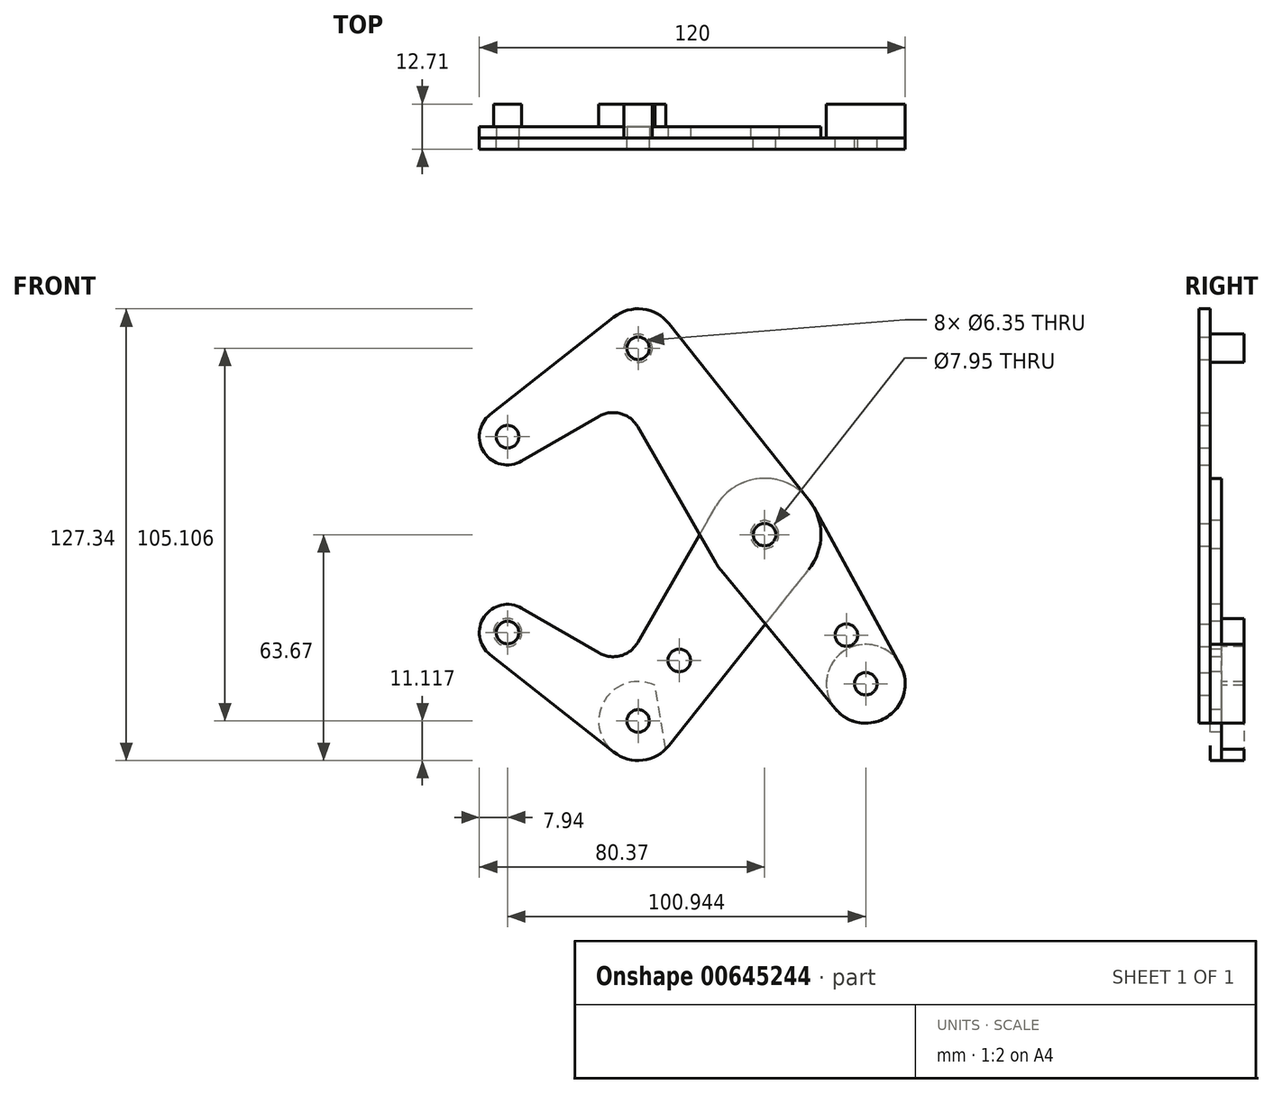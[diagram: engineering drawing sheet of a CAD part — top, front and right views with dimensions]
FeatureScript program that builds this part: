
annotation { "Feature Type Name" : "Feature", "Feature Type Description" : "" }
export const myFeature = defineFeature(function(context is Context, id is Id, definition is map)
    precondition{}
    {
        {
            var Q0;
            Q0=qCreatedBy(makeId("Front.planeOp"),FACE);
            var sketch = newSketch(context, id + "F0", { "sketchPlane" : qUnion([Q0])});
            skLineSegment(sketch, "E0", {"start": v(-35.64, 52.55) * mm, "end": v(-72.43, 27.6) * mm, "construction": true});
            skLineSegment(sketch, "E1", {"start": v(-35.64, 52.55) * mm, "end": v(28.51, -42.04) * mm, "construction": true});
            skCircle(sketch, "E2", {"center": v(-35.64, 52.55) * mm, "radius": 11.11 * mm});
            skCircle(sketch, "E3", {"center": v(-72.43, 27.6) * mm, "radius": 7.94 * mm});
            skCircle(sketch, "E4", {"center": v(-72.43, 27.6) * mm, "radius": 3.18 * mm});
            skCircle(sketch, "E5", {"center": v(-35.64, 52.55) * mm, "radius": 3.18 * mm});
            skCircle(sketch, "E6", {"center": v(0, 0) * mm, "radius": 15.88 * mm});
            skCircle(sketch, "E7", {"center": v(0, 0) * mm, "radius": 3.18 * mm});
            skCircle(sketch, "E8", {"center": v(0, 0) * mm, "radius": 3.98 * mm});
            skCircle(sketch, "E9", {"center": v(28.51, -42.04) * mm, "radius": 11.11 * mm});
            skCircle(sketch, "E10", {"center": v(28.51, -42.04) * mm, "radius": 3.18 * mm});
            skCircle(sketch, "E11", {"center": v(23.05, -28.33) * mm, "radius": 3.18 * mm});
            skLineSegment(sketch, "E12", {"start": v(0, 0) * mm, "end": v(-35.64, -52.55) * mm, "construction": true});
            skLineSegment(sketch, "E13", {"start": v(-77.34, 33.84) * mm, "end": v(-42.52, 61.28) * mm});
            skLineSegment(sketch, "E14", {"start": v(-68.46, 20.73) * mm, "end": v(-46.64, 33.35) * mm});
            skLineSegment(sketch, "E15", {"start": v(-26.94, 59.46) * mm, "end": v(12.43, 9.87) * mm});
            skLineSegment(sketch, "E16", {"start": v(-35.76, 30.43) * mm, "end": v(-13.77, -7.9) * mm});
            skLineSegment(sketch, "E17", {"start": v(-12.25, -10.1) * mm, "end": v(19.94, -49.11) * mm});
            skLineSegment(sketch, "E18", {"start": v(38.26, -36.7) * mm, "end": v(13.92, 7.64) * mm});
            skArc(sketch, "E19.filletArc", {"start": v(-35.76, 30.43) * mm, "mid": v(-40.6, 34.15) * mm, "end": v(-46.64, 33.35) * mm});
            skCircle(sketch, "E20", {"center": v(-35.64, -52.55) * mm, "radius": 3.18 * mm});
            skCircle(sketch, "E21", {"center": v(-35.64, -52.55) * mm, "radius": 11.11 * mm});
            skCircle(sketch, "E22", {"center": v(-24.05, -35.46) * mm, "radius": 3.18 * mm});
            skLineSegment(sketch, "E23", {"start": v(-35.64, -52.55) * mm, "end": v(-72.43, -27.6) * mm, "construction": true});
            skCircle(sketch, "E24", {"center": v(-72.43, -27.6) * mm, "radius": 7.94 * mm});
            skCircle(sketch, "E25", {"center": v(-72.43, -27.6) * mm, "radius": 3.18 * mm});
            skLineSegment(sketch, "E26", {"start": v(-68.46, -20.73) * mm, "end": v(-46.64, -33.35) * mm});
            skLineSegment(sketch, "E27", {"start": v(-77.34, -33.84) * mm, "end": v(-42.52, -61.28) * mm});
            skLineSegment(sketch, "E28", {"start": v(-35.76, -30.43) * mm, "end": v(-13.77, 7.9) * mm});
            skLineSegment(sketch, "E29", {"start": v(-26.94, -59.46) * mm, "end": v(12.43, -9.87) * mm});
            skArc(sketch, "E30.filletArc", {"start": v(-46.64, -33.35) * mm, "mid": v(-40.6, -34.15) * mm, "end": v(-35.76, -30.43) * mm});
            skSolve(sketch);
        }
        {
            var Q0;
            {var subQ4=sQuery(id+"F0.wireOp",EDGE,"E13");Q0=makeQuery(id+"F0.imprint","IMPRINT",FACE,{"disambiguationData":[TD([[makeQuery(id+"F0.imprint","IMPRINT",EDGE,{"derivedFrom":subQ4}),-1.0]])]});}
            var Q1;
            Q1=makeQuery(id+"F0.imprint","IMPRINT",FACE,{"disambiguationData":[TD([[makeQuery(id+"F0.imprint","IMPRINT",EDGE,{"derivedFrom":sQuery(id+"F0.wireOp",EDGE,"E4")}),-1.0]])]});
            var Q2;
            Q2=makeQuery(id+"F0.imprint","IMPRINT",FACE,{"disambiguationData":[TD([[makeQuery(id+"F0.imprint","IMPRINT",EDGE,{"derivedFrom":sQuery(id+"F0.wireOp",EDGE,"E5")}),-1.0]])]});
            var Q3;
            Q3=makeQuery(id+"F0.imprint","IMPRINT",FACE,{"disambiguationData":[TD([[makeQuery(id+"F0.imprint","IMPRINT",EDGE,{"derivedFrom":sQuery(id+"F0.wireOp",EDGE,"E8")}),-1.0]])]});
            var Q4;
            Q4=makeQuery(id+"F0.imprint","IMPRINT",FACE,{"disambiguationData":[TD([[makeQuery(id+"F0.imprint","IMPRINT",EDGE,{"derivedFrom":sQuery(id+"F0.wireOp",EDGE,"E11")}),-1.0]])]});
            var Q5;
            Q5=makeQuery(id+"F0.imprint","IMPRINT",FACE,{"disambiguationData":[TD([[makeQuery(id+"F0.imprint","IMPRINT",EDGE,{"derivedFrom":sQuery(id+"F0.wireOp",EDGE,"E10")}),-1.0]])]});
            var Q6;
            Q6=makeQuery(id+"F0.imprint","IMPRINT",FACE,{"disambiguationData":[TD([[makeQuery(id+"F0.imprint","IMPRINT",EDGE,{"derivedFrom":sQuery(id+"F0.wireOp",EDGE,"E7")}),-1.0]])]});
            var Q7;
            {var subQ0=sQuery(id+"F0.wireOp",EDGE,"E17");var subQ1=sQuery(id+"F0.wireOp",EDGE,"E6");var subQ2=makeQuery(id+"F0.imprint","INTERSECT",VERTEX,{"derivedFrom":[subQ1,subQ0]});Q7=makeQuery(id+"F0.imprint","IMPRINT",FACE,{"disambiguationData":[TD([[makeQuery(id+"F0.imprint","IMPRINT",EDGE,{"disambiguationData":[TD([[subQ2,-1.0]])],"derivedFrom":subQ1}),-1.0]])]});}
            var Q8;
            {var subQ0=sQuery(id+"F0.wireOp",EDGE,"E16");var subQ1=sQuery(id+"F0.wireOp",EDGE,"E6");var subQ2=makeQuery(id+"F0.imprint","INTERSECT",VERTEX,{"derivedFrom":[subQ1,subQ0]});Q8=makeQuery(id+"F0.imprint","IMPRINT",FACE,{"disambiguationData":[TD([[makeQuery(id+"F0.imprint","IMPRINT",EDGE,{"disambiguationData":[TD([[subQ2,1.0]])],"derivedFrom":subQ1}),-1.0]])]});}
            extrude(context, id + "F1", {"entities" : qUnion([Q0, Q1, Q2, Q3, Q4, Q5, Q6, Q7, Q8]), "depth" : 3.17 * mm, "offsetDistance" : 25.4 * mm});
        }
        {
            var Q0;
            Q0=makeQuery(id+"F0.imprint","IMPRINT",FACE,{"disambiguationData":[TD([[makeQuery(id+"F0.imprint","IMPRINT",EDGE,{"derivedFrom":sQuery(id+"F0.wireOp",EDGE,"E25")}),-1.0]])]});
            var Q1;
            Q1=makeQuery(id+"F0.imprint","IMPRINT",FACE,{"disambiguationData":[TD([[makeQuery(id+"F0.imprint","IMPRINT",EDGE,{"derivedFrom":sQuery(id+"F0.wireOp",EDGE,"E22")}),-1.0]])]});
            var Q2;
            Q2=makeQuery(id+"F0.imprint","IMPRINT",FACE,{"disambiguationData":[TD([[makeQuery(id+"F0.imprint","IMPRINT",EDGE,{"derivedFrom":sQuery(id+"F0.wireOp",EDGE,"E20")}),-1.0]])]});
            var Q3;
            {var subQ0=sQuery(id+"F0.wireOp",EDGE,"E17");var subQ1=sQuery(id+"F0.wireOp",EDGE,"E6");var subQ2=makeQuery(id+"F0.imprint","INTERSECT",VERTEX,{"derivedFrom":[subQ1,subQ0]});Q3=makeQuery(id+"F0.imprint","IMPRINT",FACE,{"disambiguationData":[TD([[makeQuery(id+"F0.imprint","IMPRINT",EDGE,{"disambiguationData":[TD([[subQ2,-1.0]])],"derivedFrom":subQ1}),-1.0]])]});}
            var Q4;
            {var subQ0=sQuery(id+"F0.wireOp",EDGE,"E16");var subQ1=sQuery(id+"F0.wireOp",EDGE,"E6");var subQ2=makeQuery(id+"F0.imprint","INTERSECT",VERTEX,{"derivedFrom":[subQ1,subQ0]});Q4=makeQuery(id+"F0.imprint","IMPRINT",FACE,{"disambiguationData":[TD([[makeQuery(id+"F0.imprint","IMPRINT",EDGE,{"disambiguationData":[TD([[subQ2,1.0]])],"derivedFrom":subQ1}),-1.0]])]});}
            var Q5;
            Q5=makeQuery(id+"F0.imprint","IMPRINT",FACE,{"disambiguationData":[TD([[makeQuery(id+"F0.imprint","IMPRINT",EDGE,{"derivedFrom":sQuery(id+"F0.wireOp",EDGE,"E8")}),-1.0]])]});
            extrude(context, id + "F2", {"entities" : qUnion([Q0, Q1, Q2, Q3, Q4, Q5]), "oppositeDirection" : true, "depth" : 3.17 * mm, "offsetDistance" : 25.4 * mm});
        }
        {
            var Q0;
            Q0=makeQuery(id+"F1.opExtrude","CAP_FACE",FACE,{"disambiguationData":[OSD([sQuery(id+"F0.wireOp",EDGE,"E2"),sQuery(id+"F0.wireOp",EDGE,"E3"),sQuery(id+"F0.wireOp",EDGE,"E4"),sQuery(id+"F0.wireOp",EDGE,"E5"),sQuery(id+"F0.wireOp",EDGE,"E6"),sQuery(id+"F0.wireOp",EDGE,"E7"),sQuery(id+"F0.wireOp",EDGE,"E9"),sQuery(id+"F0.wireOp",EDGE,"E10"),sQuery(id+"F0.wireOp",EDGE,"E11"),sQuery(id+"F0.wireOp",EDGE,"E13"),sQuery(id+"F0.wireOp",EDGE,"E14"),sQuery(id+"F0.wireOp",EDGE,"E15"),sQuery(id+"F0.wireOp",EDGE,"E16"),sQuery(id+"F0.wireOp",EDGE,"E17"),sQuery(id+"F0.wireOp",EDGE,"E18"),sQuery(id+"F0.wireOp",EDGE,"E19.filletArc")])],"isStart":false});
            var sketch = newSketch(context, id + "F3", { "sketchPlane" : qUnion([Q0])});
            skCircle(sketch, "E31", {"center": v(-35.64, 52.55) * mm, "radius": 3.98 * mm});
            skCircle(sketch, "E32.0", {"center": v(28.51, -42.04) * mm, "radius": 11.11 * mm});
            skSolve(sketch);
        }
        {
            var Q0;
            Q0=makeQuery(id+"F0.imprint","IMPRINT",FACE,{"disambiguationData":[TD([[makeQuery(id+"F0.imprint","IMPRINT",EDGE,{"derivedFrom":sQuery(id+"F0.wireOp",EDGE,"E22")}),-1.0]])]});
            var sketch = newSketch(context, id + "F4", { "sketchPlane" : qUnion([Q0])});
            skCircle(sketch, "E33", {"center": v(-72.43, -27.6) * mm, "radius": 3.98 * mm});
            skArc(sketch, "E34.0", {"start": v(-30.85, -42.53) * mm, "mid": v(-46.6, -54.35) * mm, "end": v(-27.9, -60.53) * mm});
            skLineSegment(sketch, "E35", {"start": v(-35.64, -52.55) * mm, "end": v(28.51, -42.04) * mm, "construction": true});
            skLineSegment(sketch, "E36", {"start": v(-30.85, -42.53) * mm, "end": v(-27.9, -60.53) * mm});
            skSolve(sketch);
        }
        {
            var Q0;
            Q0=qCreatedBy(makeId("Front.planeOp"),FACE);
            cPlane(context, id + "F5", {"entities" : qUnion([Q0]), "cplaneType" : CPlaneType.OFFSET, "offset" : 9.52 * mm, "oppositeDirection" : true, "width" : 152.4 * mm, "height" : 152.4 * mm});
        }
        {
            var Q0;
            Q0 = qSketchRegion(id + "F3", true);
            var Q1;
            Q1 = qSketchRegion(id + "F4", true);
            var Q2;
            Q2=qCreatedBy(id+"F5.planeOp",FACE);
            extrude(context, id + "F6", {"entities" : qUnion([Q0, Q1]), "endBound" : BoundingType.UP_TO_SURFACE, "oppositeDirection" : true, "depth" : 25.4 * mm, "endBoundEntityFace" : qUnion([Q2]), "offsetDistance" : 25.4 * mm});
        }
        {
            var Q0;
            Q0=makeQuery(id+"F1.opExtrude","SWEPT_BODY",BODY,{"disambiguationData":[OSD([sQuery(id+"F0.wireOp",EDGE,"E2"),sQuery(id+"F0.wireOp",EDGE,"E3"),sQuery(id+"F0.wireOp",EDGE,"E4"),sQuery(id+"F0.wireOp",EDGE,"E5"),sQuery(id+"F0.wireOp",EDGE,"E6"),sQuery(id+"F0.wireOp",EDGE,"E7"),sQuery(id+"F0.wireOp",EDGE,"E9"),sQuery(id+"F0.wireOp",EDGE,"E10"),sQuery(id+"F0.wireOp",EDGE,"E11"),sQuery(id+"F0.wireOp",EDGE,"E13"),sQuery(id+"F0.wireOp",EDGE,"E14"),sQuery(id+"F0.wireOp",EDGE,"E15"),sQuery(id+"F0.wireOp",EDGE,"E16"),sQuery(id+"F0.wireOp",EDGE,"E17"),sQuery(id+"F0.wireOp",EDGE,"E18"),sQuery(id+"F0.wireOp",EDGE,"E19.filletArc")])]});
            var Q1;
            Q1=makeQuery(id+"F2.opExtrude","SWEPT_BODY",BODY,{"disambiguationData":[OSD([sQuery(id+"F0.wireOp",EDGE,"E6"),sQuery(id+"F0.wireOp",EDGE,"E8"),sQuery(id+"F0.wireOp",EDGE,"E20"),sQuery(id+"F0.wireOp",EDGE,"E21"),sQuery(id+"F0.wireOp",EDGE,"E22"),sQuery(id+"F0.wireOp",EDGE,"E24"),sQuery(id+"F0.wireOp",EDGE,"E25"),sQuery(id+"F0.wireOp",EDGE,"E26"),sQuery(id+"F0.wireOp",EDGE,"E27"),sQuery(id+"F0.wireOp",EDGE,"E28"),sQuery(id+"F0.wireOp",EDGE,"E29"),sQuery(id+"F0.wireOp",EDGE,"E30.filletArc")])]});
            var Q2;
            Q2=makeQuery(id+"F6.opExtrude","SWEPT_BODY",BODY,{"disambiguationData":[OSD([sQuery(id+"F3.wireOp",EDGE,"E32.0")])]});
            var Q3;
            Q3=makeQuery(id+"F6.opExtrude","SWEPT_BODY",BODY,{"disambiguationData":[OSD([sQuery(id+"F4.wireOp",EDGE,"E34.0"),sQuery(id+"F4.wireOp",EDGE,"E36")])]});
            var Q4;
            Q4=makeQuery(id+"F6.opExtrude","SWEPT_BODY",BODY,{"disambiguationData":[OSD([sQuery(id+"F4.wireOp",EDGE,"E33")])]});
            var Q5;
            Q5=makeQuery(id+"F6.opExtrude","SWEPT_BODY",BODY,{"disambiguationData":[OSD([sQuery(id+"F3.wireOp",EDGE,"E31")])]});
            booleanBodies(context, id + "F7", {"operationType" : BooleanOperationType.SUBTRACTION, "tools" : qUnion([Q0, Q1]), "targets" : qUnion([Q2, Q3, Q4, Q5]), "keepTools" : true});
        }
    });
